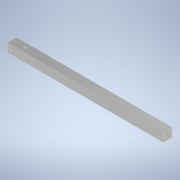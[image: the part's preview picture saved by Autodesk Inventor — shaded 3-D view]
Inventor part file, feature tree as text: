
AUTODESK INVENTOR PART (.ipt)
format: ipt  version: 2020.3 (Build 243373000, 373)  size: 134,656 bytes
history: native  units: mm
features: sketch x3, hole x2, other x1, extrude x1
ambient origin geometry x8: Origin, YZ Plane, XZ Plane, XY Plane, X Axis, Y Axis, Z Axis, Center Point
bodies: Body1 (feature_tree)
feature tree (7):
  other  "ソリッド1"
  extrude  "押し出し1"  Depth=9.0mm
  hole  "穴1"  [1 undecoded]
  hole  "穴2"  [1 undecoded]
  sketch  "スケッチ1"
  sketch  "スケッチ2"
  sketch  "スケッチ3"
note: 2 required parameter values undecoded (feature->parameter linkage not recoverable at this tier; creation-order binding heuristic only, values carry confidence <= 0.55)
